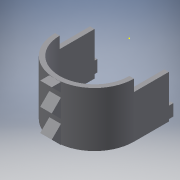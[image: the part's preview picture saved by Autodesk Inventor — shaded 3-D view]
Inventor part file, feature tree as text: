
AUTODESK INVENTOR PART (.ipt)
format: ipt  version: 2016 (Build 200138000, 138)  size: 235,008 bytes
history: native  units: in
note: dims shown in document units (in); Inventor stores cm internally (conversion verified against a paired STEP export)
features: sketch x11, extrude x10, reference x10, plane x1
ambient origin geometry x8: Origin, YZ Plane, XZ Plane, XY Plane, X Axis, Y Axis, Z Axis, Center Point
bodies: Solid1 (feature_tree)
feature tree (32):
  extrude  "Extrusion1"  Depth=1.5in TaperAngle=0.0deg
  extrude  "Extrusion2"  Depth=0.1969in TaperAngle=0.0deg
  extrude  "Extrusion3"  [1 undecoded]
  extrude  "Extrusion4"  Depth=0.3937in
  plane  "Work Plane1"
  sketch  "Sketch5"  dims[d12=1.9685in d14=0.9774in d15=0.3937in d17=1.0in d19=0.5in d20=0.0in]
  extrude  "Extrusion5"  Depth=0.5in TaperAngle=0.0deg
  extrude  "Extrusion6"  Depth=0.197in TaperAngle=0.0deg
  extrude  "Extrusion7"  Depth=16.0in TaperAngle=0.0deg
  extrude  "Extrusion8"  Depth=0.5in TaperAngle=0.0deg
  extrude  "Extrusion9"  [1 undecoded]
  extrude  "Extrusion10"  [1 undecoded]
  sketch  "Sketch1"  dims[d0=0.1969in d1=1.5in d2=0.0in]
  reference  "Reference1"
  sketch  "Sketch2"  dims[d3=4.6969in d4=0.0in d5=0.1969in d6=0.0in]
  sketch  "Sketch3"  dims[d7=0.1969in d8=0.0in d9=-1.697in]
  sketch  "Sketch4"  dims[d10=0.7874in d11=0.3937in]
  reference  "Reference2"
  sketch  "Sketch6"  dims[d21=0.197in d22=0.0in d23=2.0in d24=0.0in]
  sketch  "Sketch8"  dims[d25=2.0in d26=0.0in d27=16.0in d28=0.0in]
  reference  "Reference3"
  reference  "Reference5"
  reference  "Reference6"
  reference  "Reference7"
  reference  "Reference8"
  reference  "Reference9"
  sketch  "Sketch9"  dims[d29=0.5in d30=6575.0in d31=0.0in]
  reference  "Reference10"
  sketch  "Sketch10"
  reference  "Reference11"
  sketch  "Sketch11"
  sketch  "Sketch12"
note: 3 required parameter values undecoded (feature->parameter linkage not recoverable at this tier; creation-order binding heuristic only, values carry confidence <= 0.55)
